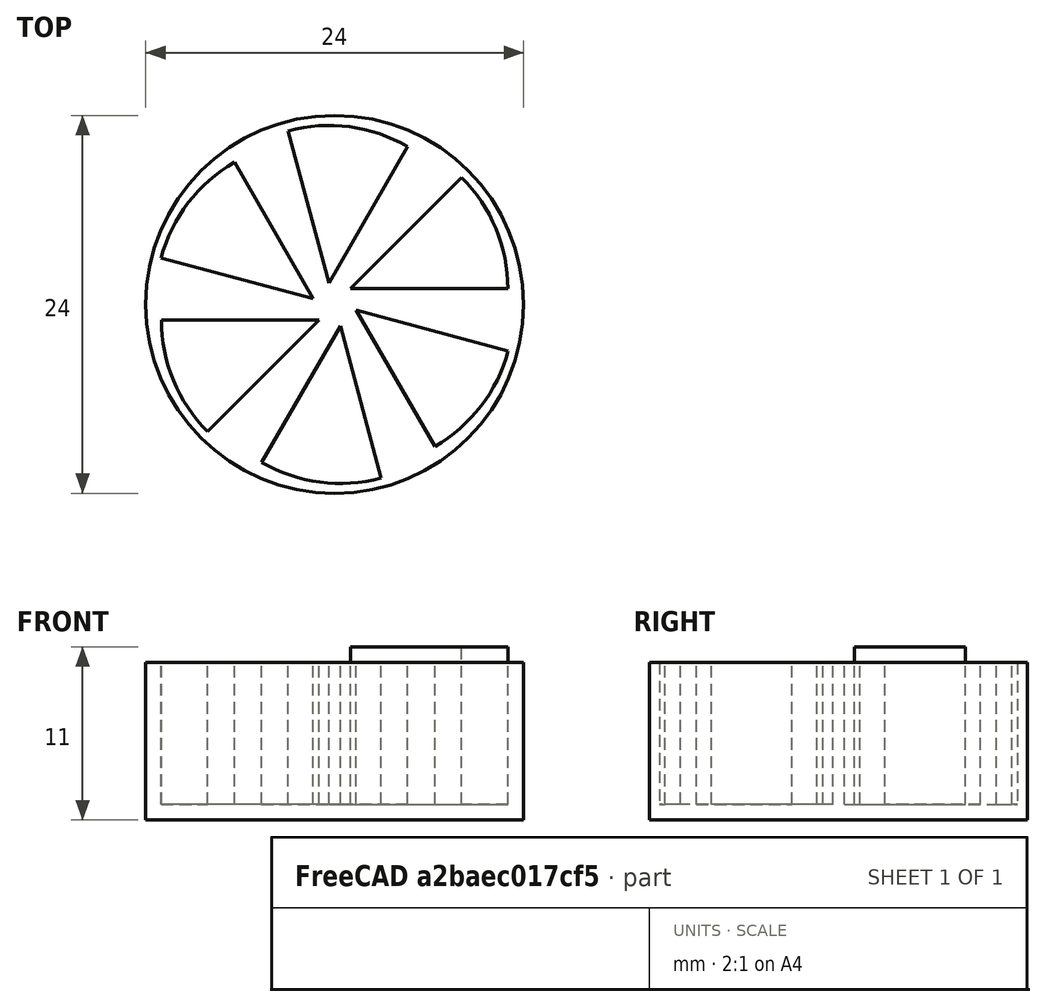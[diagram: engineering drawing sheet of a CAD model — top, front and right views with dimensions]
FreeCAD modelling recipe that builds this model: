
FCSTD DOCUMENT  (FreeCAD 0.20R29603 (Git))
Label: OJT1_T04R08_formaroda
License: All rights reserved
LicenseURL: http://en.wikipedia.org/wiki/All_rights_reserved
objects: Part::Cylinder×2, Part::FeaturePython×1, Part::Cut×1
note: 3 computed .brp shape members not serialized (recipe doc carries the construction recipe); baked Part::Feature solids carry a one-line shape summary decoded from their .brp

FEATURE [Part::Cylinder] Cylinder  label="Cilindre"
  Angle = 360
  AttacherType = Attacher::AttachEngine3D
  FirstAngle = 0
  Height = 10
  Radius = 12
  SecondAngle = 0
FEATURE [Part::Cylinder] Cylinder001  label="Cilindre001"
  Angle = 45
  AttacherType = Attacher::AttachEngine3D
  FirstAngle = 0
  Height = 10
  Placement = pos=(1,1,1) rot=(0,0,1;0rad)
  Radius = 10
  SecondAngle = 0
FEATURE [Part::FeaturePython] Array  # Draft array (typed FeaturePython)
  AlwaysSyncPlacement = false
  Angle = 360
  ArrayType = 1
  Axis = (0,0,1)
  Base = -> Cylinder001
  Center = (0,0,0)
  Count = 6
  ExpandArray = false
  Fuse = false
  IntervalAxis = (0,0,0)
  IntervalX = (50,0,0)
  IntervalY = (0,50,0)
  IntervalZ = (0,0,50)
  NumberCircles = 3
  NumberPolar = 6
  NumberX = 2
  NumberY = 2
  NumberZ = 1
  PlacementList = 6 placements: [(1,1,1),(-0.366025,1.36603,1),(-1.36603,0.366025,1),(-1,-1,1),(0.366025,-1.36603,1),(1.36603,-0.366025,1)]
  RadialDistance = 50
  ScaleList = (6) [(1,1,1),(1,1,1),(1,1,1),(1,1,1),(1,1,1),(1,1,1)]
  Symmetry = 1
  TangentialDistance = 25
FEATURE [Part::Cut] Cut
  Base = -> Cylinder
  Tool = -> Array
